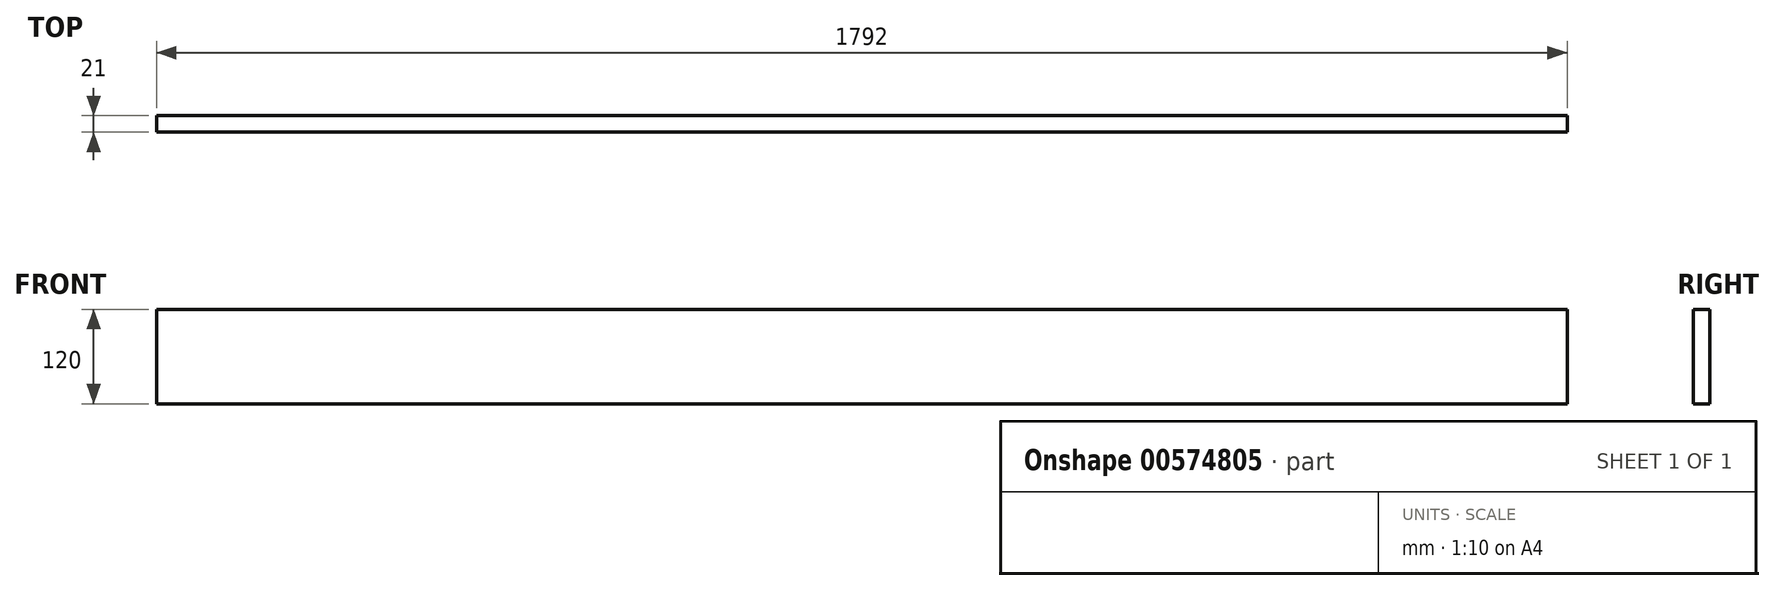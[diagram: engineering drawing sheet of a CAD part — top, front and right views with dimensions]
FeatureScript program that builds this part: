
annotation { "Feature Type Name" : "Feature", "Feature Type Description" : "" }
export const myFeature = defineFeature(function(context is Context, id is Id, definition is map)
    precondition{}
    {
        {
            var Q0;
            Q0=qCreatedBy(makeId("Right.planeOp"),FACE);
            var sketch = newSketch(context, id + "F0", { "sketchPlane" : qUnion([Q0])});
            skLineSegment(sketch, "E0.bottom", {"start": v(-10.5, 60) * mm, "end": v(10.5, 60) * mm});
            skLineSegment(sketch, "E0.top", {"start": v(-10.5, -60) * mm, "end": v(10.5, -60) * mm});
            skLineSegment(sketch, "E0.left", {"start": v(-10.5, 60) * mm, "end": v(-10.5, -60) * mm});
            skLineSegment(sketch, "E0.right", {"start": v(10.5, 60) * mm, "end": v(10.5, -60) * mm});
            skSolve(sketch);
        }
        {
            var Q0;
            Q0=makeQuery(id+"F0.imprint","IMPRINT",FACE,{"disambiguationData":[TD([[makeQuery(id+"F0.imprint","IMPRINT",EDGE,{"derivedFrom":sQuery(id+"F0.wireOp",EDGE,"E0.bottom")}),-1.0]])]});
            extrude(context, id + "F1", {"entities" : qUnion([Q0]), "depth" : 1792 * mm, "offsetDistance" : 25 * mm});
        }
    });
